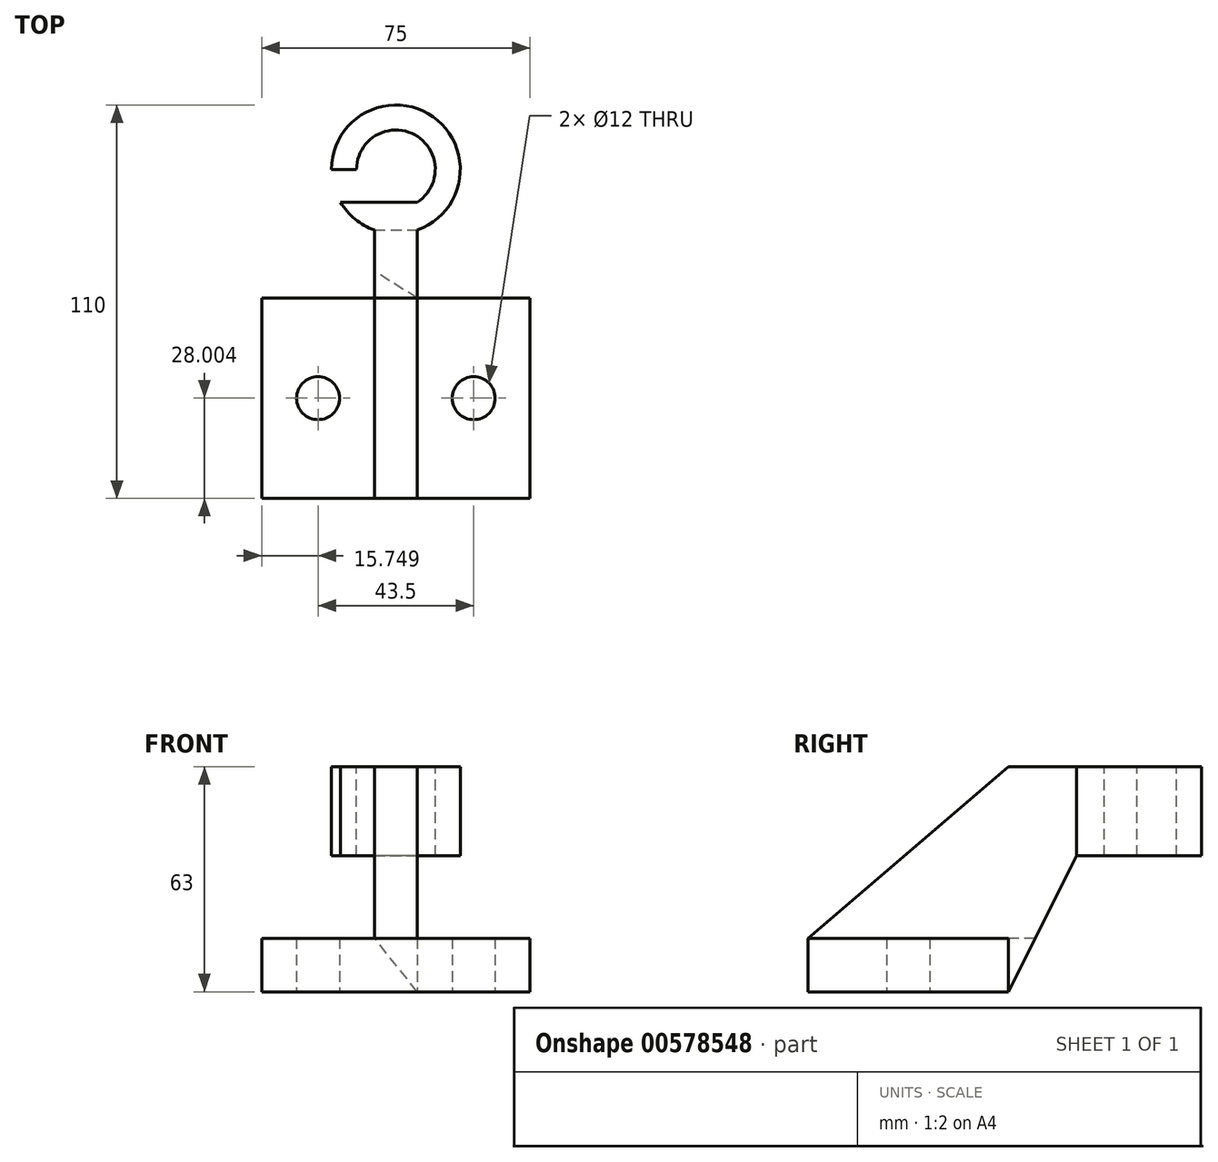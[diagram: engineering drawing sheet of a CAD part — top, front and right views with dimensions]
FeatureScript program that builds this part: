
annotation { "Feature Type Name" : "Feature", "Feature Type Description" : "" }
export const myFeature = defineFeature(function(context is Context, id is Id, definition is map)
    precondition{}
    {
        {
            var Q0;
            Q0=qCreatedBy(makeId("Top.planeOp"),FACE);
            var sketch = newSketch(context, id + "F0", { "sketchPlane" : qUnion([Q0])});
            skLineSegment(sketch, "E0.bottom", {"start": v(-41.74, 26.56) * mm, "end": v(33.26, 26.56) * mm});
            skLineSegment(sketch, "E0.top", {"start": v(-41.74, -29.44) * mm, "end": v(33.26, -29.44) * mm});
            skLineSegment(sketch, "E0.left", {"start": v(-41.74, 26.56) * mm, "end": v(-41.74, -29.44) * mm});
            skLineSegment(sketch, "E0.right", {"start": v(33.26, 26.56) * mm, "end": v(33.26, -29.44) * mm});
            skLineSegment(sketch, "E1", {"start": v(-4.24, -29.44) * mm, "end": v(1.76, -29.44) * mm});
            skLineSegment(sketch, "E2", {"start": v(1.76, -29.44) * mm, "end": v(-10.24, -29.44) * mm});
            skLineSegment(sketch, "E3", {"start": v(-10.24, -29.44) * mm, "end": v(-10.24, 26.56) * mm});
            skLineSegment(sketch, "E4", {"start": v(-10.24, 26.56) * mm, "end": v(1.76, 26.56) * mm});
            skLineSegment(sketch, "E5", {"start": v(1.76, 26.56) * mm, "end": v(1.76, -29.44) * mm});
            skLineSegment(sketch, "E6", {"start": v(-41.74, -29.44) * mm, "end": v(-41.74, -1.44) * mm});
            skLineSegment(sketch, "E7", {"start": v(-41.74, -1.44) * mm, "end": v(-10.24, -1.44) * mm});
            skCircle(sketch, "E8", {"center": v(-26, -1.44) * mm, "radius": 6 * mm});
            skLineSegment(sketch, "E9", {"start": v(1.76, -1.44) * mm, "end": v(33.26, -1.44) * mm});
            skCircle(sketch, "E10", {"center": v(17.5, -1.44) * mm, "radius": 6 * mm});
            skSolve(sketch);
        }
        {
            var Q0;
            Q0 = qSketchRegion(id + "F0", true);
            extrude(context, id + "F1", {"entities" : qUnion([Q0]), "depth" : 15 * mm, "offsetDistance" : 25 * mm});
        }
        {
            var Q0;
            Q0=makeQuery(id+"F1.opExtrude","CAP_FACE",FACE,{"disambiguationData":[OSD([sQuery(id+"F0.wireOp",EDGE,"E0.bottom"),sQuery(id+"F0.wireOp",EDGE,"E0.top"),sQuery(id+"F0.wireOp",EDGE,"E0.left"),sQuery(id+"F0.wireOp",EDGE,"E0.right"),sQuery(id+"F0.wireOp",EDGE,"E2"),sQuery(id+"F0.wireOp",EDGE,"E4"),sQuery(id+"F0.wireOp",EDGE,"E6"),sQuery(id+"F0.wireOp",EDGE,"E8"),sQuery(id+"F0.wireOp",EDGE,"E10")])],"isStart":false});
            var sketch = newSketch(context, id + "F2", { "sketchPlane" : qUnion([Q0])});
            skLineSegment(sketch, "E11.0.0", {"start": v(33.26, -29.44) * mm, "end": v(33.26, 26.56) * mm});
            skLineSegment(sketch, "E11.0.1", {"start": v(33.26, 26.56) * mm, "end": v(-41.74, 26.56) * mm});
            skLineSegment(sketch, "E11.0.2", {"start": v(-41.74, 26.56) * mm, "end": v(-41.74, -29.44) * mm});
            skLineSegment(sketch, "E11.0.3", {"start": v(-41.74, -29.44) * mm, "end": v(33.26, -29.44) * mm});
            skLineSegment(sketch, "E12.0", {"start": v(-10.24, -29.44) * mm, "end": v(-10.24, 26.56) * mm});
            skLineSegment(sketch, "E13.0", {"start": v(1.76, 26.56) * mm, "end": v(1.76, -29.44) * mm});
            skSolve(sketch);
        }
        {
            var Q0;
            {var subQ0=sQuery(id+"F2.wireOp",EDGE,"E12.0");Q0=makeQuery(id+"F2.imprint","IMPRINT",FACE,{"disambiguationData":[TD([[makeQuery(id+"F2.imprint","IMPRINT",EDGE,{"derivedFrom":subQ0}),-1.0]])]});}
            extrude(context, id + "F3", {"entities" : qUnion([Q0]), "operationType" : NewBodyOperationType.ADD, "depth" : (63 - 15) * mm, "offsetDistance" : 25 * mm});
        }
        {
            var Q0;
            Q0=makeQuery(id+"F3.opExtrude","SWEPT_FACE",FACE,{"disambiguationData":[OSD([sQuery(id+"F2.wireOp",EDGE,"E13.0")])]});
            var sketch = newSketch(context, id + "F4", { "sketchPlane" : qUnion([Q0])});
            skLineSegment(sketch, "E14", {"start": v(26.56, 63) * mm, "end": v(-29.44, 15) * mm});
            skSolve(sketch);
        }
        {
            var Q0;
            Q0 = qSketchRegion(id + "F4", true);
            var Q1;
            Q1=makeQuery(id+"F4.imprint","IMPRINT",FACE,{"disambiguationData":[TD([[makeQuery(id+"F4.imprint","IMPRINT",EDGE,{"derivedFrom":sQuery(id+"F4.wireOp",EDGE,"E14")}),-1.0]])]});
            extrude(context, id + "F5", {"entities" : qUnion([Q0, Q1]), "operationType" : NewBodyOperationType.REMOVE, "oppositeDirection" : true, "depth" : 25 * mm, "offsetDistance" : 25 * mm});
        }
        {
            var Q0;
            Q0=makeQuery(id+"F3.boolean.opBoolean","MERGE",FACE,{"derivedFrom":[makeQuery(id+"F1.opExtrude","SWEPT_FACE",FACE,{"disambiguationData":[OSD([sQuery(id+"F0.wireOp",EDGE,"E0.bottom"),sQuery(id+"F0.wireOp",EDGE,"E4")])]}),makeQuery(id+"F3.opExtrude","SWEPT_FACE",FACE,{"disambiguationData":[OSD([sQuery(id+"F2.wireOp",EDGE,"E11.0.1")])]})]});
            var sketch = newSketch(context, id + "F6", { "sketchPlane" : qUnion([Q0])});
            skLineSegment(sketch, "E15", {"start": v(-1.76, 15) * mm, "end": v(-1.76, 0) * mm});
            skLineSegment(sketch, "E16", {"start": v(-1.76, 0) * mm, "end": v(10.24, 15) * mm});
            skLineSegment(sketch, "E17", {"start": v(10.24, 15) * mm, "end": v(10.24, 0) * mm});
            skSolve(sketch);
        }
        {
            var Q0;
            Q0 = qSketchRegion(id + "F6", true);
            var Q1;
            Q1=makeQuery(id+"F6.imprint","IMPRINT",FACE,{"disambiguationData":[TD([[makeQuery(id+"F6.imprint","IMPRINT",EDGE,{"derivedFrom":sQuery(id+"F6.wireOp",EDGE,"E15")}),1.0]])]});
            extrude(context, id + "F7", {"entities" : qUnion([Q0, Q1]), "operationType" : NewBodyOperationType.ADD, "depth" : 36 * mm, "offsetDistance" : 25 * mm});
        }
        {
            var Q0;
            Q0=makeQuery(id+"F7.opExtrude","SWEPT_FACE",FACE,{"disambiguationData":[OSD([sQuery(id+"F2.wireOp",EDGE,"E11.0.1"),sQuery(id+"F2.wireOp",EDGE,"E13.0"),sQuery(id+"F4.wireOp",EDGE,"E14")])]});
            var sketch = newSketch(context, id + "F8", { "sketchPlane" : qUnion([Q0])});
            skCircle(sketch, "E18", {"center": v(-4.24, 62.56) * mm, "radius": 18 * mm});
            skCircle(sketch, "E19", {"center": v(-4.24, 62.56) * mm, "radius": 11 * mm});
            skSolve(sketch);
        }
        {
            var Q0;
            Q0 = qSketchRegion(id + "F8", true);
            extrude(context, id + "F9", {"entities" : qUnion([Q0]), "operationType" : NewBodyOperationType.ADD, "oppositeDirection" : true, "depth" : 25 * mm, "offsetDistance" : 25 * mm});
        }
        {
            var Q0;
            {var subQ0=sQuery(id+"F2.wireOp",EDGE,"E13.0");Q0=makeQuery(id+"F7.boolean.opBoolean","MERGE",FACE,{"derivedFrom":[makeQuery(id+"F3.opExtrude","SWEPT_FACE",FACE,{"disambiguationData":[OSD([subQ0])]}),makeQuery(id+"F7.opExtrude","SWEPT_FACE",FACE,{"disambiguationData":[OSD([sQuery(id+"F2.wireOp",EDGE,"E11.0.1"),subQ0,sQuery(id+"F6.wireOp",EDGE,"E15")])]})]});}
            var sketch = newSketch(context, id + "F10", { "sketchPlane" : qUnion([Q0])});
            skLineSegment(sketch, "E20", {"start": v(26.56, 0) * mm, "end": v(45.6, 38) * mm});
            skSolve(sketch);
        }
        {
            var Q0;
            Q0 = qSketchRegion(id + "F10", true);
            var Q1;
            Q1=makeQuery(id+"F10.imprint","IMPRINT",FACE,{"disambiguationData":[TD([[makeQuery(id+"F10.imprint","IMPRINT",EDGE,{"derivedFrom":sQuery(id+"F10.wireOp",EDGE,"E20")}),-1.0]])]});
            extrude(context, id + "F11", {"entities" : qUnion([Q0, Q1]), "operationType" : NewBodyOperationType.REMOVE, "oppositeDirection" : true, "depth" : 25 * mm, "offsetDistance" : 25 * mm});
        }
    });
